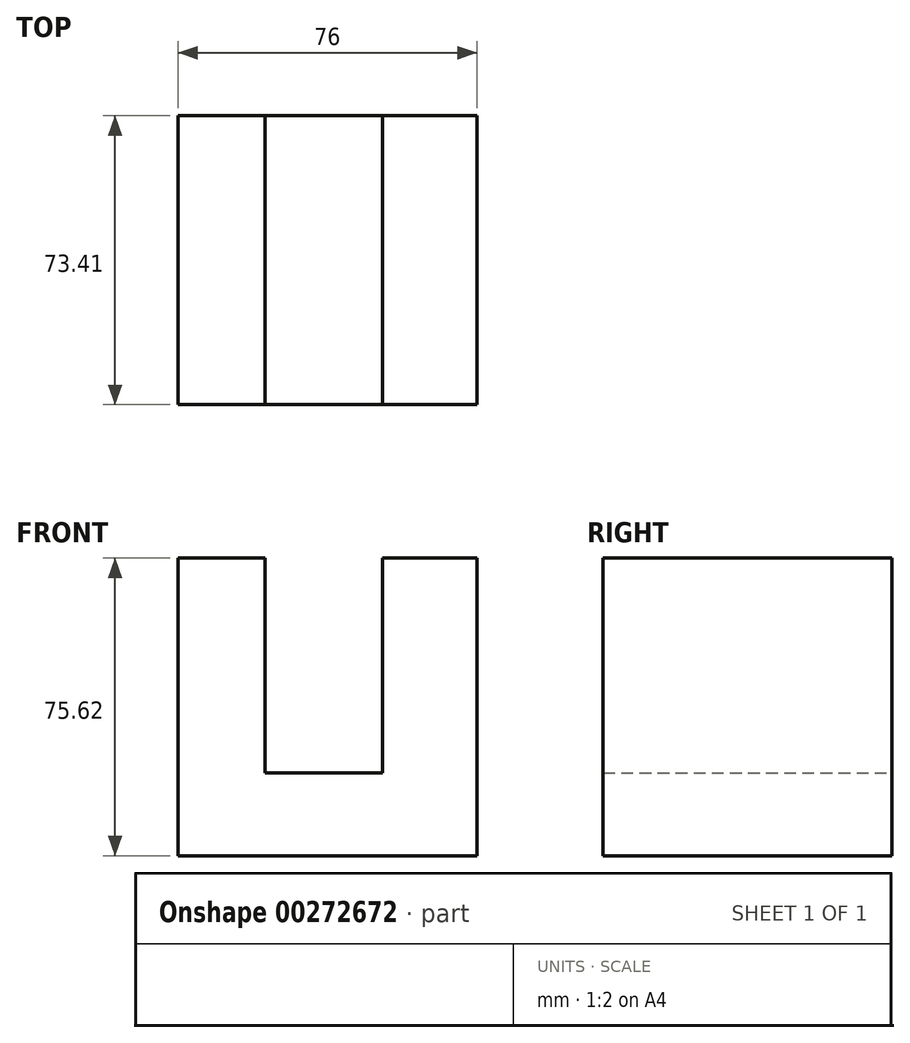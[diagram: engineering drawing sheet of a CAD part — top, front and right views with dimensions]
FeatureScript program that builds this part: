
annotation { "Feature Type Name" : "Feature", "Feature Type Description" : "" }
export const myFeature = defineFeature(function(context is Context, id is Id, definition is map)
    precondition{}
    {
        {
            var Q0;
            Q0=qCreatedBy(makeId("Front.planeOp"),FACE);
            var sketch = newSketch(context, id + "F0", { "sketchPlane" : qUnion([Q0])});
            skLineSegment(sketch, "E0", {"start": v(0, 0) * mm, "end": v(-76, 0) * mm});
            skLineSegment(sketch, "E1", {"start": v(-76, 0) * mm, "end": v(-76, 75.62) * mm});
            skLineSegment(sketch, "E2", {"start": v(-76, 75.62) * mm, "end": v(-53.85, 75.62) * mm});
            skLineSegment(sketch, "E3", {"start": v(-53.85, 75.62) * mm, "end": v(-53.85, 21) * mm});
            skLineSegment(sketch, "E4", {"start": v(-53.85, 21) * mm, "end": v(-24.06, 21) * mm});
            skLineSegment(sketch, "E5", {"start": v(-24.06, 21) * mm, "end": v(-24.06, 75.62) * mm});
            skLineSegment(sketch, "E6", {"start": v(-24.06, 75.62) * mm, "end": v(0, 75.62) * mm});
            skLineSegment(sketch, "E7", {"start": v(0, 75.62) * mm, "end": v(0, 0) * mm});
            skSolve(sketch);
        }
        {
            var Q0;
            Q0 = qSketchRegion(id + "F0", true);
            extrude(context, id + "F1", {"entities" : qUnion([Q0]), "depth" : 73.4 * mm});
        }
    });
